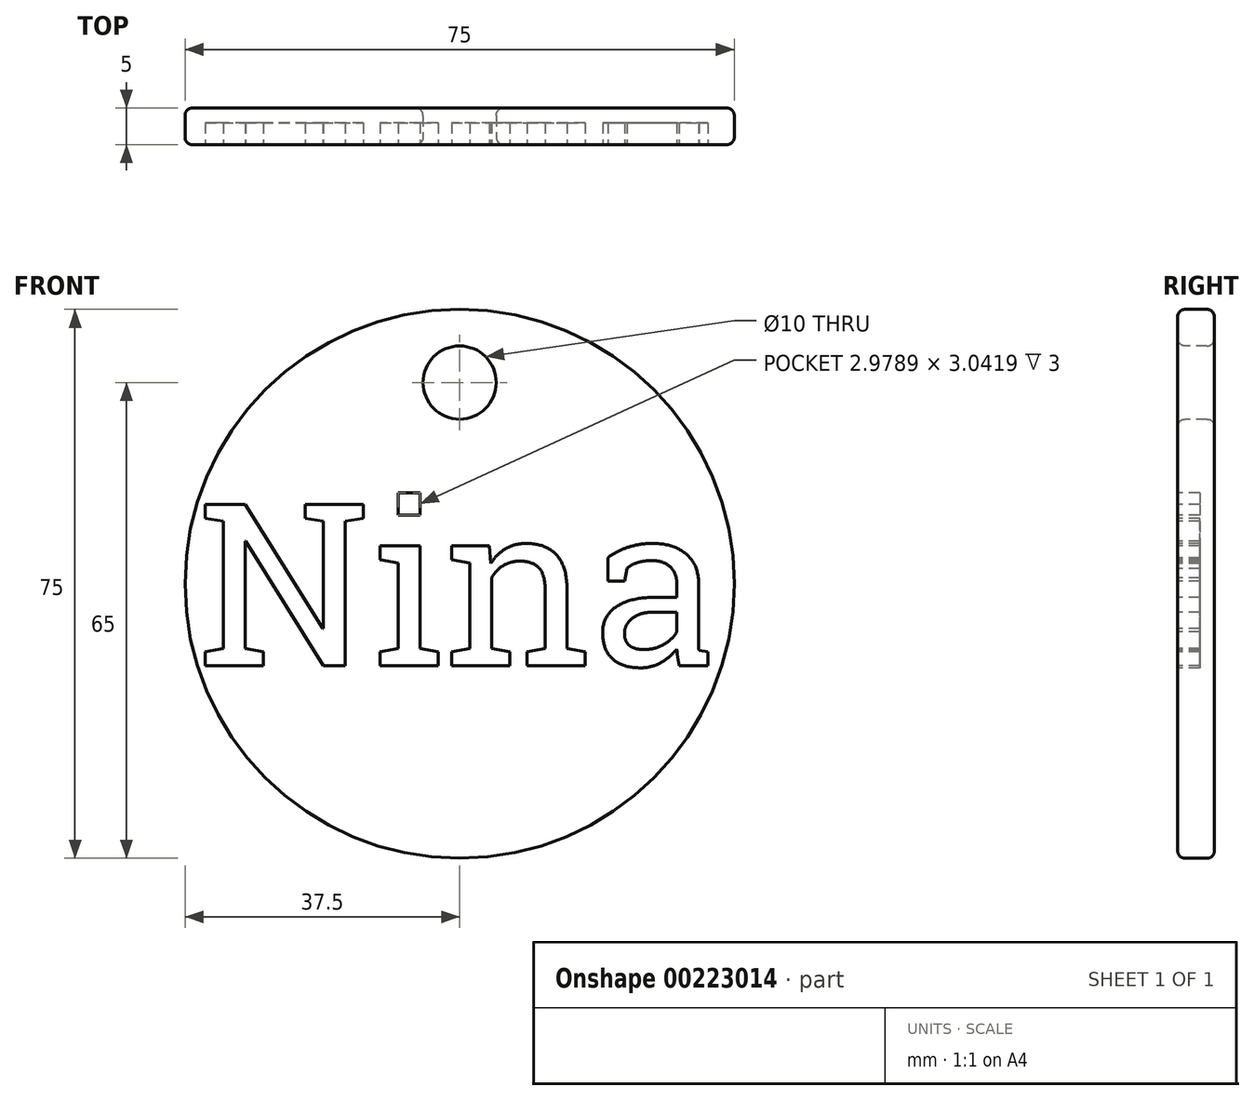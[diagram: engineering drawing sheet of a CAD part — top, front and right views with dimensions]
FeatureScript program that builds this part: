
annotation { "Feature Type Name" : "Feature", "Feature Type Description" : "" }
export const myFeature = defineFeature(function(context is Context, id is Id, definition is map)
    precondition{}
    {
        {
            var Q0;
            Q0=qCreatedBy(makeId("Front.planeOp"),FACE);
            var sketch = newSketch(context, id + "F0", { "sketchPlane" : qUnion([Q0])});
            skCircle(sketch, "E0", {"center": v(0, 0) * mm, "radius": 37.5 * mm});
            skText(sketch, "E1", { "text": "Nina", "fontName": "RobotoSlab-Regular.ttf"});
            skCircle(sketch, "E2", {"center": v(0, 27.5) * mm, "radius": 5 * mm});
            const initialGuessF0  = {"E1": [-0.0358, -0.01116, 1, 0, 0.02232]};
            skSetInitialGuess(sketch, initialGuessF0);
            skSolve(sketch);
        }
        {
            var Q0;
            Q0=makeQuery(id+"F0.imprint","IMPRINT",FACE,{"disambiguationData":[TD([[makeQuery(id+"F0.imprint","IMPRINT",EDGE,{"derivedFrom":sQuery(id+"F0.wireOp",EDGE,"E1.sketch_text.stroke-0")}),-1.0]])]});
            var Q1;
            Q1=makeQuery(id+"F0.imprint","IMPRINT",FACE,{"disambiguationData":[TD([[makeQuery(id+"F0.imprint","IMPRINT",EDGE,{"derivedFrom":sQuery(id+"F0.wireOp",EDGE,"E1.sketch_text.stroke-24")}),-1.0]])]});
            var Q2;
            Q2=makeQuery(id+"F0.imprint","IMPRINT",FACE,{"disambiguationData":[TD([[makeQuery(id+"F0.imprint","IMPRINT",EDGE,{"derivedFrom":sQuery(id+"F0.wireOp",EDGE,"E1.sketch_text.stroke-34")}),-1.0]])]});
            var Q3;
            Q3=makeQuery(id+"F0.imprint","IMPRINT",FACE,{"disambiguationData":[TD([[makeQuery(id+"F0.imprint","IMPRINT",EDGE,{"derivedFrom":sQuery(id+"F0.wireOp",EDGE,"E1.sketch_text.stroke-38")}),-1.0]])]});
            var Q4;
            Q4=makeQuery(id+"F0.imprint","IMPRINT",FACE,{"disambiguationData":[TD([[makeQuery(id+"F0.imprint","IMPRINT",EDGE,{"derivedFrom":sQuery(id+"F0.wireOp",EDGE,"E1.sketch_text.stroke-64")}),-1.0]])]});
            var Q5;
            Q5=makeQuery(id+"F0.imprint","IMPRINT",FACE,{"disambiguationData":[TD([[makeQuery(id+"F0.imprint","IMPRINT",EDGE,{"derivedFrom":sQuery(id+"F0.wireOp",EDGE,"E0")}),1.0]])]});
            var Q6;
            Q6=makeQuery(id+"F0.imprint","IMPRINT",FACE,{"disambiguationData":[TD([[makeQuery(id+"F0.imprint","IMPRINT",EDGE,{"derivedFrom":sQuery(id+"F0.wireOp",EDGE,"E1.sketch_text.stroke-91")}),1.0]])]});
            extrude(context, id + "F1", {"entities" : qUnion([Q0, Q1, Q2, Q3, Q4, Q5, Q6]), "oppositeDirection" : true, "depth" : 5 * mm});
        }
        {
            var Q0;
            Q0=makeQuery(id+"F0.imprint","IMPRINT",FACE,{"disambiguationData":[TD([[makeQuery(id+"F0.imprint","IMPRINT",EDGE,{"derivedFrom":sQuery(id+"F0.wireOp",EDGE,"E1.sketch_text.stroke-0")}),-1.0]])]});
            var Q1;
            Q1=makeQuery(id+"F0.imprint","IMPRINT",FACE,{"disambiguationData":[TD([[makeQuery(id+"F0.imprint","IMPRINT",EDGE,{"derivedFrom":sQuery(id+"F0.wireOp",EDGE,"E1.sketch_text.stroke-24")}),-1.0]])]});
            var Q2;
            Q2=makeQuery(id+"F0.imprint","IMPRINT",FACE,{"disambiguationData":[TD([[makeQuery(id+"F0.imprint","IMPRINT",EDGE,{"derivedFrom":sQuery(id+"F0.wireOp",EDGE,"E1.sketch_text.stroke-34")}),-1.0]])]});
            var Q3;
            Q3=makeQuery(id+"F0.imprint","IMPRINT",FACE,{"disambiguationData":[TD([[makeQuery(id+"F0.imprint","IMPRINT",EDGE,{"derivedFrom":sQuery(id+"F0.wireOp",EDGE,"E1.sketch_text.stroke-38")}),-1.0]])]});
            var Q4;
            Q4=makeQuery(id+"F0.imprint","IMPRINT",FACE,{"disambiguationData":[TD([[makeQuery(id+"F0.imprint","IMPRINT",EDGE,{"derivedFrom":sQuery(id+"F0.wireOp",EDGE,"E1.sketch_text.stroke-64")}),-1.0]])]});
            extrude(context, id + "F2", {"entities" : qUnion([Q0, Q1, Q2, Q3, Q4]), "operationType" : NewBodyOperationType.REMOVE, "oppositeDirection" : true, "depth" : 3 * mm});
        }
        {
            var Q0;
            Q0=makeQuery(id+"F1.opExtrude","CAP_EDGE",EDGE,{"disambiguationData":[OSD([sQuery(id+"F0.wireOp",EDGE,"E0")])],"isStart":true});
            var Q1;
            Q1=makeQuery(id+"F1.opExtrude","CAP_EDGE",EDGE,{"disambiguationData":[OSD([sQuery(id+"F0.wireOp",EDGE,"E0")])],"isStart":false});
            var Q2;
            Q2=makeQuery(id+"F1.opExtrude","CAP_EDGE",EDGE,{"disambiguationData":[OSD([sQuery(id+"F0.wireOp",EDGE,"E2")])],"isStart":true});
            var Q3;
            Q3=makeQuery(id+"F1.opExtrude","CAP_EDGE",EDGE,{"disambiguationData":[OSD([sQuery(id+"F0.wireOp",EDGE,"E2")])],"isStart":false});
            fillet(context, id + "F3", {"entities" : qUnion([Q0, Q1, Q2, Q3]), "radius" : 1 * mm, "tangentPropagation" : true, "allowEdgeOverflow" : false});
        }
    });
